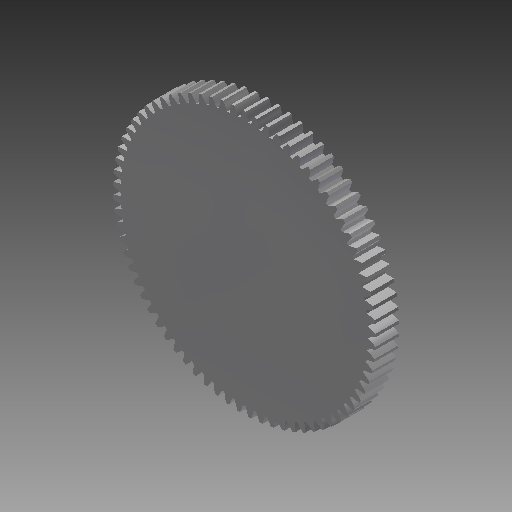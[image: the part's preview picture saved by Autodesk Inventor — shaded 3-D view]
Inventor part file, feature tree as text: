
AUTODESK INVENTOR PART (.ipt)
format: ipt  version: 2019 (Build 230136000, 136)  size: 441,856 bytes
history: native  units: mm (DEFAULTED — no unit token found)
features: plane x3, other x3, sketch x2, extrude x1
ambient origin geometry x8: Origin, YZ Plane, XZ Plane, XY Plane, X Axis, Y Axis, Z Axis, Center Point
bodies: Solid1 (feature_tree)
feature tree (9):
  extrude  "Extrusion1"  Depth=10.0mm TaperAngle=0.0deg
  plane  "Work Plane2"
  plane  "Work Plane8"
  plane  "Work Plane9"
  other  "正齒輪"
  sketch  "Sketch1"  dims[d0=112.5mm d1=10.0mm d2=0.0mm]
  sketch  "Sketch2"  dims[d3=107.647568mm d4=10.0mm d5=0.0mm d16=32.441733mm d17=0.0mm d34=0.430355mm d39=0.0mm d41=0.0mm d43=32.441733mm d46=32.441733mm d47=0.0mm d48=0.0mm]
  other  "Srf1"
  other  "節圓直徑"
